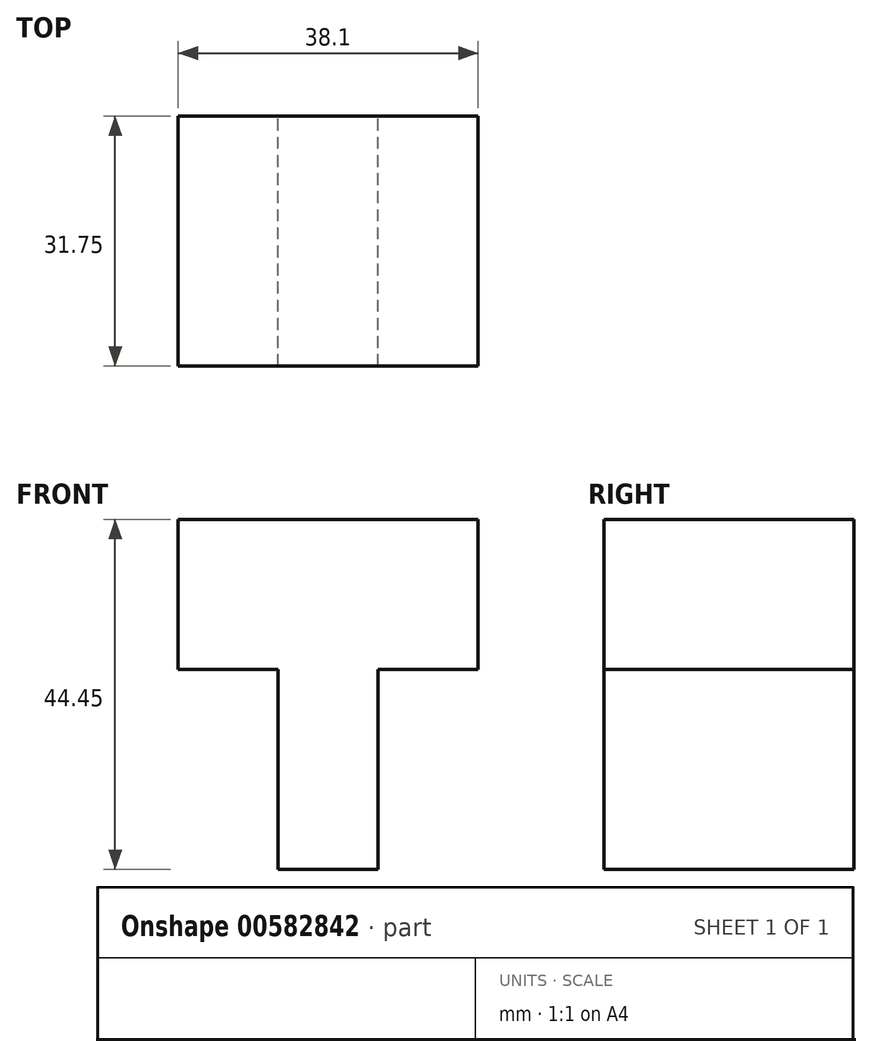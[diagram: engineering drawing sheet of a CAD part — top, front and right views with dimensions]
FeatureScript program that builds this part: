
annotation { "Feature Type Name" : "Feature", "Feature Type Description" : "" }
export const myFeature = defineFeature(function(context is Context, id is Id, definition is map)
    precondition{}
    {
        {
            var Q0;
            Q0=qCreatedBy(makeId("Front.planeOp"),FACE);
            var sketch = newSketch(context, id + "F0", { "sketchPlane" : qUnion([Q0])});
            skLineSegment(sketch, "E0", {"start": v(-62.03, 65.43) * mm, "end": v(-62.03, 46.38) * mm});
            skLineSegment(sketch, "E1", {"start": v(-62.03, 46.38) * mm, "end": v(-49.33, 46.38) * mm});
            skLineSegment(sketch, "E2", {"start": v(-49.33, 46.38) * mm, "end": v(-49.33, 20.98) * mm});
            skLineSegment(sketch, "E3", {"start": v(-49.33, 20.98) * mm, "end": v(-36.63, 20.98) * mm});
            skLineSegment(sketch, "E4", {"start": v(-36.63, 20.98) * mm, "end": v(-36.63, 46.38) * mm});
            skLineSegment(sketch, "E5", {"start": v(-36.63, 46.38) * mm, "end": v(-23.93, 46.38) * mm});
            skLineSegment(sketch, "E6", {"start": v(-23.93, 46.38) * mm, "end": v(-23.93, 65.43) * mm});
            skLineSegment(sketch, "E7", {"start": v(-23.93, 65.43) * mm, "end": v(-62.03, 65.43) * mm});
            skSolve(sketch);
        }
        {
            var Q0;
            Q0 = qSketchRegion(id + "F0", true);
            extrude(context, id + "F1", {"entities" : qUnion([Q0]), "depth" : 31.75 * mm, "offsetDistance" : 25.4 * mm});
        }
    });
